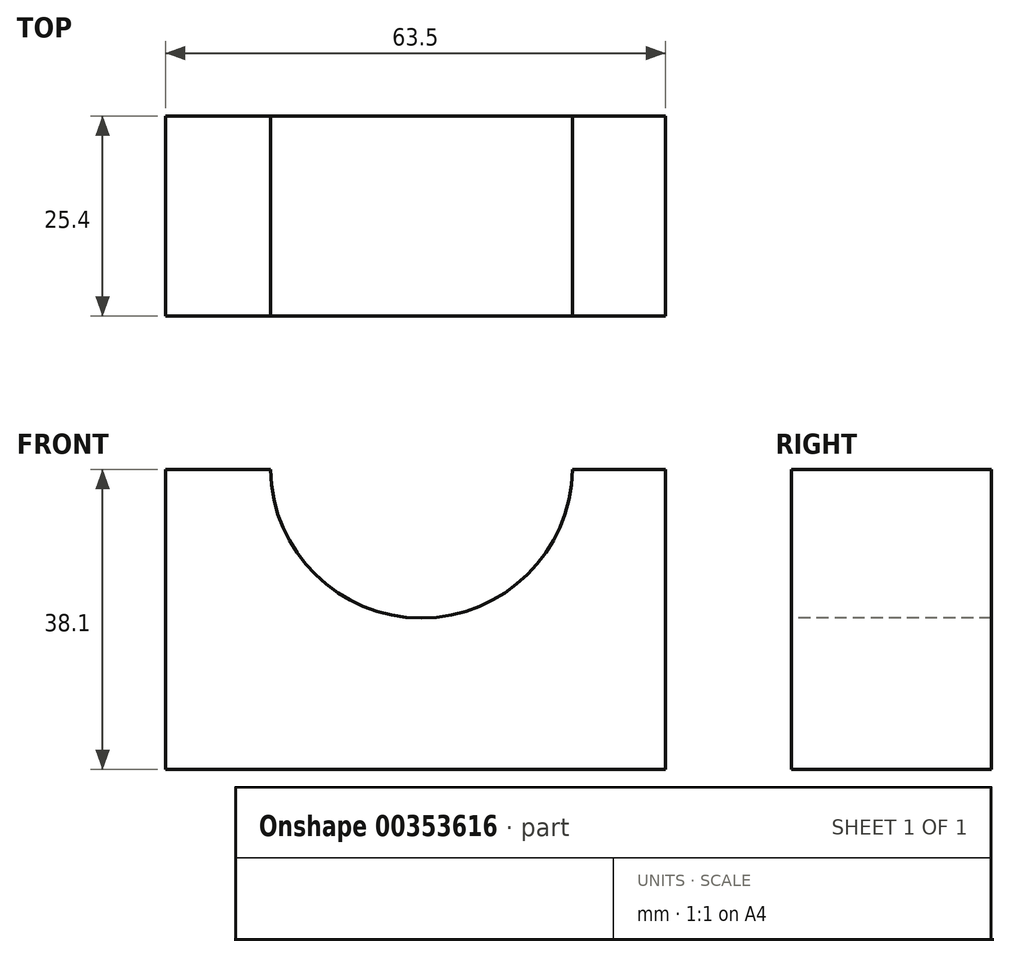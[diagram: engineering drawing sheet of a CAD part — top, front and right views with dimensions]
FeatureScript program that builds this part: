
annotation { "Feature Type Name" : "Feature", "Feature Type Description" : "" }
export const myFeature = defineFeature(function(context is Context, id is Id, definition is map)
    precondition{}
    {
        {
            var Q0;
            Q0=qCreatedBy(makeId("Front.planeOp"),FACE);
            var sketch = newSketch(context, id + "F0", { "sketchPlane" : qUnion([Q0])});
            skLineSegment(sketch, "E0.bottom", {"start": v(0, 0) * mm, "end": v(63.5, 0) * mm});
            skLineSegment(sketch, "E0.top", {"start": v(0, 38.1) * mm, "end": v(63.5, 38.1) * mm});
            skLineSegment(sketch, "E0.left", {"start": v(0, 0) * mm, "end": v(0, 38.1) * mm});
            skLineSegment(sketch, "E0.right", {"start": v(63.5, 0) * mm, "end": v(63.5, 38.1) * mm});
            skSolve(sketch);
        }
        {
            var Q0;
            Q0 = qSketchRegion(id + "F0", true);
            extrude(context, id + "F1", {"entities" : qUnion([Q0]), "depth" : 25.4 * mm});
        }
        {
            var Q0;
            Q0=makeQuery(id+"F1.opExtrude","CAP_FACE",FACE,{"disambiguationData":[OSD([sQuery(id+"F0.wireOp",EDGE,"E0.bottom"),sQuery(id+"F0.wireOp",EDGE,"E0.top"),sQuery(id+"F0.wireOp",EDGE,"E0.left"),sQuery(id+"F0.wireOp",EDGE,"E0.right")])],"isStart":false});
            var sketch = newSketch(context, id + "F2", { "sketchPlane" : qUnion([Q0])});
            skArc(sketch, "E1", {"start": v(13.3, 38.1) * mm, "mid": v(32.5, 19.24) * mm, "end": v(51.69, 38.1) * mm});
            skLineSegment(sketch, "E2", {"start": v(13.3, 38.1) * mm, "end": v(51.69, 38.1) * mm});
            skSolve(sketch);
        }
        {
            var Q0;
            Q0=makeQuery(id+"F2.imprint","IMPRINT",FACE,{"disambiguationData":[TD([[makeQuery(id+"F2.imprint","IMPRINT",EDGE,{"derivedFrom":sQuery(id+"F2.wireOp",EDGE,"E1")}),1.0]])]});
            extrude(context, id + "F3", {"entities" : qUnion([Q0]), "operationType" : NewBodyOperationType.REMOVE, "oppositeDirection" : true, "depth" : 25.4 * mm});
        }
    });
